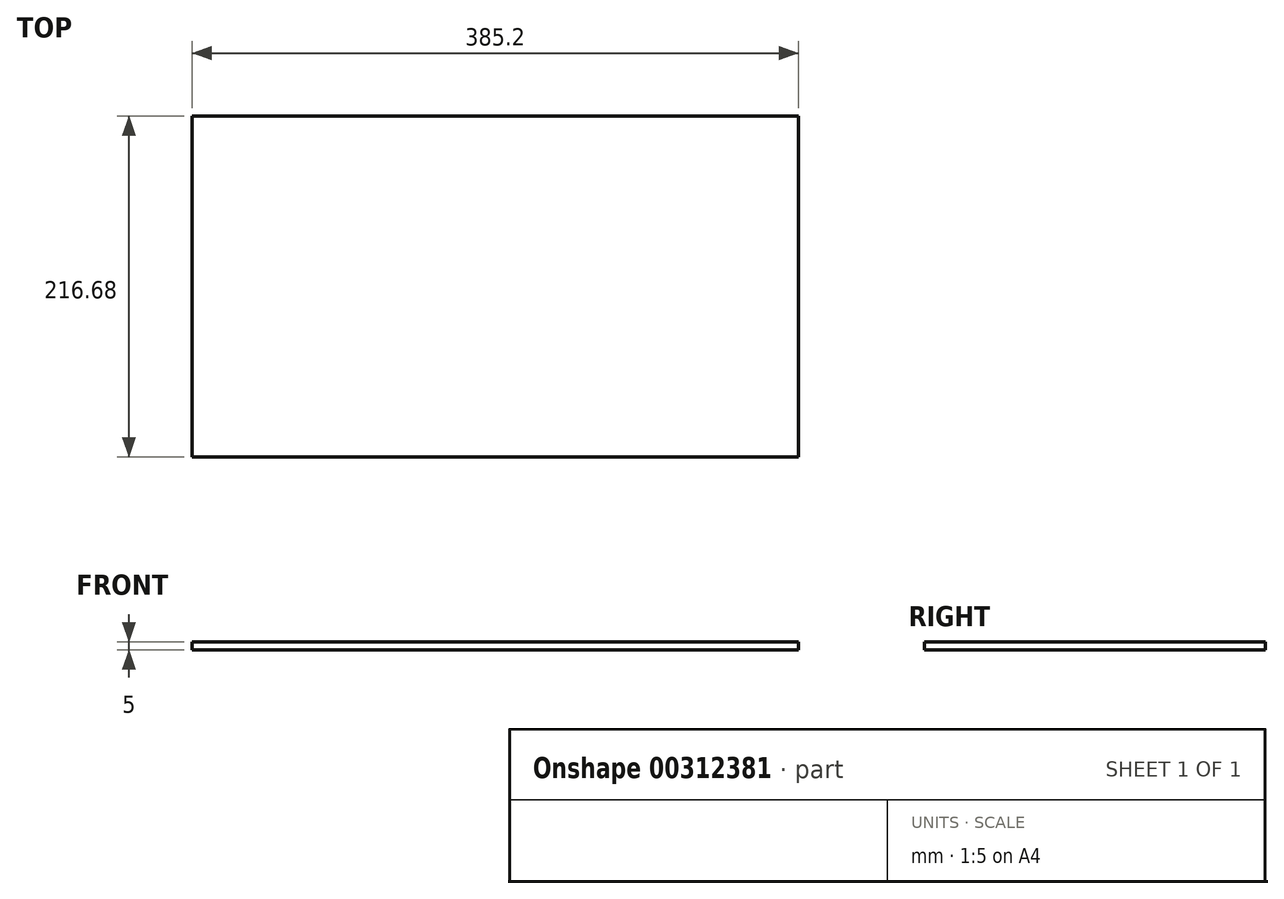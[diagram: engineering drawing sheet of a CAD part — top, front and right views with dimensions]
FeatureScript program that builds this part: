
annotation { "Feature Type Name" : "Feature", "Feature Type Description" : "" }
export const myFeature = defineFeature(function(context is Context, id is Id, definition is map)
    precondition{}
    {
        {
            var Q0;
            Q0=qCreatedBy(makeId("Top.planeOp"),FACE);
            var sketch = newSketch(context, id + "F0", { "sketchPlane" : qUnion([Q0])});
            skLineSegment(sketch, "E0.bottom", {"start": v(192.6, -108.34) * mm, "end": v(-192.6, -108.34) * mm});
            skLineSegment(sketch, "E0.top", {"start": v(192.6, 108.34) * mm, "end": v(-192.6, 108.34) * mm});
            skLineSegment(sketch, "E0.left", {"start": v(192.6, -108.34) * mm, "end": v(192.6, 108.34) * mm});
            skLineSegment(sketch, "E0.right", {"start": v(-192.6, -108.34) * mm, "end": v(-192.6, 108.34) * mm});
            skPoint(sketch, "E0.middle", {"position": v(0, 0) * mm});
            skPoint(sketch, "E1", {"position": v(192.6, 108.34) * mm});
            skPoint(sketch, "E2", {"position": v(192.6, -108.34) * mm});
            skPoint(sketch, "E3", {"position": v(-192.6, -108.34) * mm});
            skPoint(sketch, "E4", {"position": v(-192.6, 108.34) * mm});
            skSolve(sketch);
        }
        {
            var Q0;
            Q0 = qSketchRegion(id + "F0", true);
            extrude(context, id + "F1", {"entities" : qUnion([Q0]), "oppositeDirection" : true, "depth" : 5 * mm});
        }
    });
